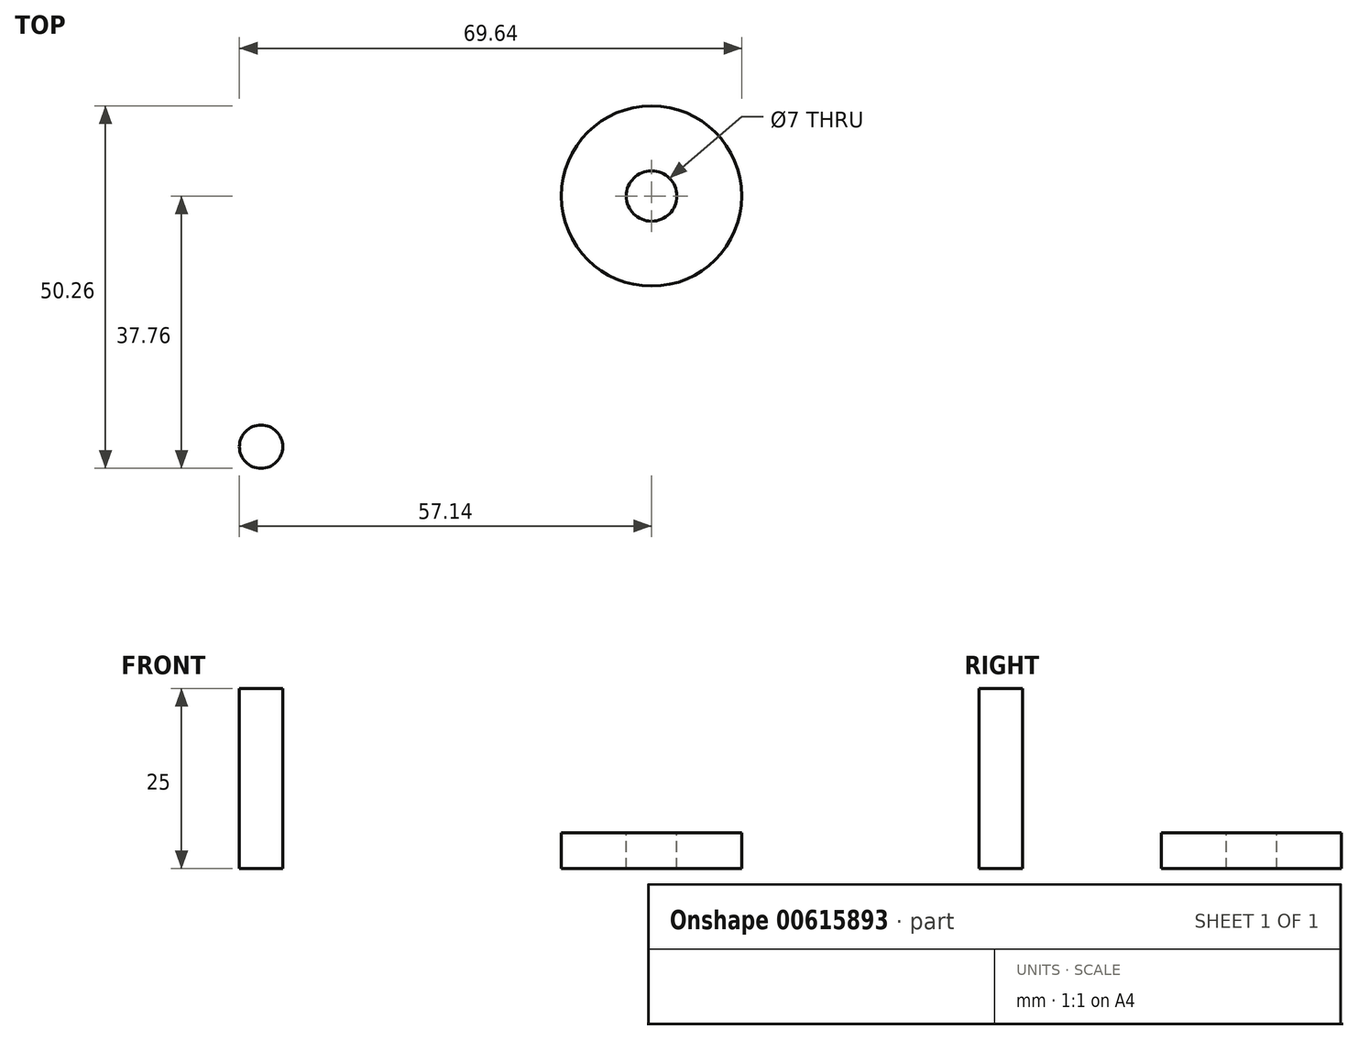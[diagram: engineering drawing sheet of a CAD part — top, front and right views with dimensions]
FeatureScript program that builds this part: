
annotation { "Feature Type Name" : "Feature", "Feature Type Description" : "" }
export const myFeature = defineFeature(function(context is Context, id is Id, definition is map)
    precondition{}
    {
        {
            var Q0;
            Q0=qCreatedBy(makeId("Top.planeOp"),FACE);
            var sketch = newSketch(context, id + "F0", { "sketchPlane" : qUnion([Q0])});
            skCircle(sketch, "E0", {"center": v(0, 0) * mm, "radius": 12.5 * mm});
            skSolve(sketch);
        }
        {
            var Q0;
            Q0=makeQuery(id+"F0.imprint","IMPRINT",FACE,{"disambiguationData":[TD([[makeQuery(id+"F0.imprint","IMPRINT",EDGE,{"derivedFrom":sQuery(id+"F0.wireOp",EDGE,"E0")}),1.0]])]});
            extrude(context, id + "F1", {"entities" : qUnion([Q0]), "depth" : 5 * mm, "offsetDistance" : 25 * mm});
        }
        {
            var Q0;
            Q0=makeQuery(id+"F1.opExtrude","CAP_FACE",FACE,{"disambiguationData":[OSD([sQuery(id+"F0.wireOp",EDGE,"E0")])],"isStart":false});
            var sketch = newSketch(context, id + "F2", { "sketchPlane" : qUnion([Q0])});
            skPoint(sketch, "E1", {"position": v(0, 0) * mm});
            skSolve(sketch);
        }
        {
            var Q0;
            Q0=sQuery(id+"F2.wireOp",VERTEX,"E1");
            var Q1;
            Q1=makeQuery(id+"F1.opExtrude","SWEPT_BODY",BODY,{"disambiguationData":[OSD([sQuery(id+"F0.wireOp",EDGE,"E0")])]});
            hole(context, id + "F3", {"style" : HoleStyle.SIMPLE, "endStyle" : HoleEndStyle.THROUGH, "holeDiameter" : 7 * mm, "majorDiameter" : 5 * mm, "isTappedThrough" : true, "tappedDepth" : 12 * mm, "tapClearance" : 3, "locations" : qUnion([Q0]), "scope" : qUnion([Q1])});
        }
        {
            var Q0;
            Q0=qCreatedBy(makeId("Top.planeOp"),FACE);
            var sketch = newSketch(context, id + "F4", { "sketchPlane" : qUnion([Q0])});
            skCircle(sketch, "E2", {"center": v(-54.14, -34.76) * mm, "radius": 3 * mm});
            skSolve(sketch);
        }
        {
            var Q0;
            Q0=makeQuery(id+"F4.imprint","IMPRINT",FACE,{"disambiguationData":[TD([[makeQuery(id+"F4.imprint","IMPRINT",EDGE,{"derivedFrom":sQuery(id+"F4.wireOp",EDGE,"E2")}),1.0]])]});
            extrude(context, id + "F5", {"entities" : qUnion([Q0]), "depth" : 25 * mm, "offsetDistance" : 25 * mm});
        }
    });
